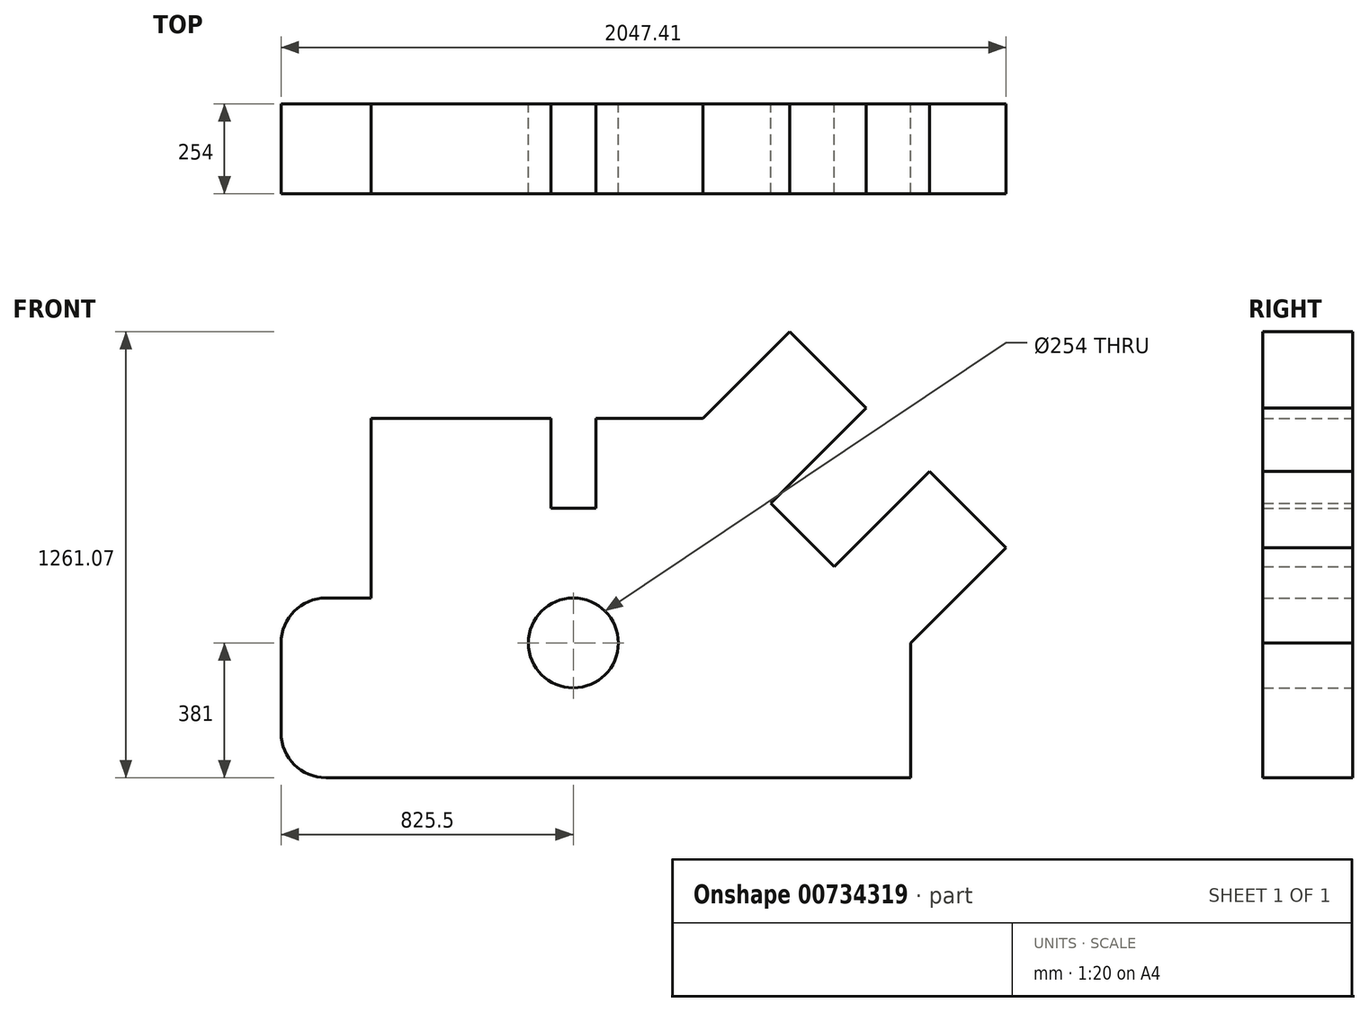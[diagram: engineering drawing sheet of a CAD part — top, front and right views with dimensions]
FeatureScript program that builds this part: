
annotation { "Feature Type Name" : "Feature", "Feature Type Description" : "" }
export const myFeature = defineFeature(function(context is Context, id is Id, definition is map)
    precondition{}
    {
        {
            var Q0;
            Q0=qCreatedBy(makeId("Front.planeOp"),FACE);
            var sketch = newSketch(context, id + "F0", { "sketchPlane" : qUnion([Q0])});
            skLineSegment(sketch, "E0", {"start": v(0, 127) * mm, "end": v(0, 381) * mm});
            skLineSegment(sketch, "E1", {"start": v(127, 0) * mm, "end": v(1778, 0) * mm});
            skLineSegment(sketch, "E2", {"start": v(1778, 0) * mm, "end": v(1778, 381) * mm});
            skLineSegment(sketch, "E3", {"start": v(1778, 381) * mm, "end": v(2047.4, 650.4) * mm});
            skLineSegment(sketch, "E4", {"start": v(2047.4, 650.4) * mm, "end": v(1831.88, 865.93) * mm});
            skLineSegment(sketch, "E5", {"start": v(1831.88, 865.93) * mm, "end": v(1562.47, 596.53) * mm});
            skLineSegment(sketch, "E6", {"start": v(1562.47, 596.53) * mm, "end": v(1382.87, 776.13) * mm});
            skLineSegment(sketch, "E7", {"start": v(1382.87, 776.13) * mm, "end": v(1652.28, 1045.54) * mm});
            skLineSegment(sketch, "E8", {"start": v(1652.28, 1045.54) * mm, "end": v(1436.75, 1261.07) * mm});
            skLineSegment(sketch, "E9", {"start": v(1436.75, 1261.07) * mm, "end": v(1167.34, 991.66) * mm});
            skLineSegment(sketch, "E10", {"start": v(127, 508) * mm, "end": v(254, 508) * mm});
            skLineSegment(sketch, "E11", {"start": v(254, 508) * mm, "end": v(254, 1016) * mm});
            skLineSegment(sketch, "E12", {"start": v(254, 1016) * mm, "end": v(762, 1016) * mm});
            skLineSegment(sketch, "E13", {"start": v(762, 1016) * mm, "end": v(762, 762) * mm});
            skLineSegment(sketch, "E14", {"start": v(762, 762) * mm, "end": v(889, 762) * mm});
            skLineSegment(sketch, "E15", {"start": v(889, 762) * mm, "end": v(889, 1016) * mm});
            skLineSegment(sketch, "E16", {"start": v(889, 1016) * mm, "end": v(1191.69, 1016) * mm});
            skLineSegment(sketch, "E17", {"start": v(1214.02, 1016) * mm, "end": v(1191.69, 1016) * mm});
            skCircle(sketch, "E18", {"center": v(825.5, 381) * mm, "radius": 127 * mm});
            skPoint(sketch, "E19.visualSharp", {"position": v(0, 0) * mm});
            skArc(sketch, "E19.filletArc", {"start": v(0, 127) * mm, "mid": v(37.2, 37.2) * mm, "end": v(127, 0) * mm});
            skPoint(sketch, "E20.visualSharp", {"position": v(0, 508) * mm});
            skArc(sketch, "E20.filletArc", {"start": v(127, 508) * mm, "mid": v(37.2, 470.8) * mm, "end": v(0, 381) * mm});
            skSolve(sketch);
        }
        {
            var Q0;
            Q0 = qSketchRegion(id + "F0", true);
            extrude(context, id + "F1", {"entities" : qUnion([Q0]), "depth" : 254 * mm, "offsetDistance" : 25.4 * mm});
        }
    });
